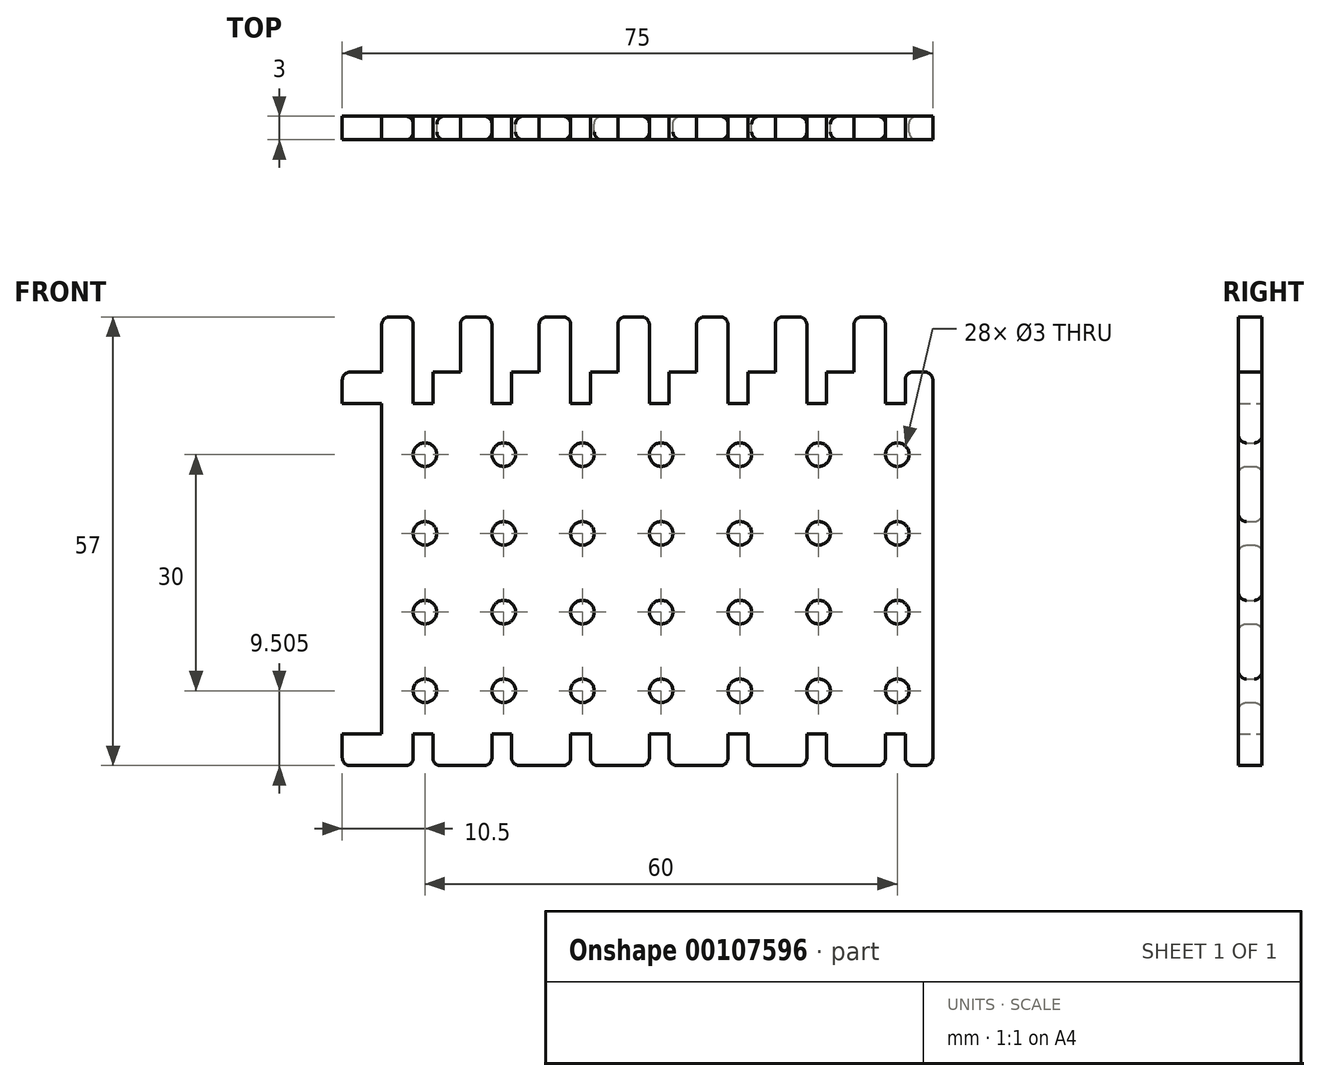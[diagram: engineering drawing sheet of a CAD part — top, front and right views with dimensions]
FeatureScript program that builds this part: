
annotation { "Feature Type Name" : "Feature", "Feature Type Description" : "" }
export const myFeature = defineFeature(function(context is Context, id is Id, definition is map)
    precondition{}
    {
        {
            var Q0;
            Q0=qCreatedBy(makeId("Front.planeOp"),FACE);
            var sketch = newSketch(context, id + "F0", { "sketchPlane" : qUnion([Q0])});
            skLineSegment(sketch, "E0.bottom", {"start": v(37.5, -25) * mm, "end": v(34, -25) * mm});
            skLineSegment(sketch, "E0.top", {"start": v(37.5, 25) * mm, "end": v(34, 25) * mm});
            skLineSegment(sketch, "E0.left", {"start": v(37.5, -25) * mm, "end": v(37.5, 25) * mm});
            skLineSegment(sketch, "E0.right", {"start": v(-37.5, -25) * mm, "end": v(-37.5, -21) * mm});
            skPoint(sketch, "E0.middle", {"position": v(0, 0) * mm});
            skLineSegment(sketch, "E1.top", {"start": v(-32.5, 32) * mm, "end": v(-28.5, 32) * mm});
            skLineSegment(sketch, "E1.left", {"start": v(-32.5, 25) * mm, "end": v(-32.5, 32) * mm});
            skLineSegment(sketch, "E1.right", {"start": v(-28.5, 25) * mm, "end": v(-28.5, 32) * mm});
            skLineSegment(sketch, "E2.top", {"start": v(-28.5, 21) * mm, "end": v(-26, 21) * mm});
            skLineSegment(sketch, "E2.left", {"start": v(-28.5, 25) * mm, "end": v(-28.5, 21) * mm});
            skLineSegment(sketch, "E2.right", {"start": v(-26, 25) * mm, "end": v(-26, 21) * mm});
            skLineSegment(sketch, "E3.top", {"start": v(-26, -21) * mm, "end": v(-28.5, -21) * mm});
            skLineSegment(sketch, "E3.left", {"start": v(-26, -25) * mm, "end": v(-26, -21) * mm});
            skLineSegment(sketch, "E3.right", {"start": v(-28.5, -25) * mm, "end": v(-28.5, -21) * mm});
            skLineSegment(sketch, "E4.bottom", {"start": v(-37.5, 21) * mm, "end": v(-32.5, 21) * mm});
            skLineSegment(sketch, "E4.top", {"start": v(-37.5, -21) * mm, "end": v(-32.5, -21) * mm});
            skLineSegment(sketch, "E4.right", {"start": v(-32.5, 21) * mm, "end": v(-32.5, -21) * mm});
            skLineSegment(sketch, "E5.trimOffspring", {"start": v(-37.5, 21) * mm, "end": v(-37.5, 25) * mm});
            skLineSegment(sketch, "E6.trimOffspring", {"start": v(-32.5, 25) * mm, "end": v(-37.5, 25) * mm});
            skLineSegment(sketch, "E7.trimOffspring", {"start": v(-28.5, -25) * mm, "end": v(-37.5, -25) * mm});
            skLineSegment(sketch, "E8.1.0.0", {"start": v(-22.5, 25) * mm, "end": v(-22.5, 32) * mm});
            skLineSegment(sketch, "E8.1.0.1", {"start": v(-22.5, 32) * mm, "end": v(-18.5, 32) * mm});
            skLineSegment(sketch, "E8.1.0.2", {"start": v(-18.5, 25) * mm, "end": v(-18.5, 32) * mm});
            skLineSegment(sketch, "E8.1.0.3", {"start": v(-18.5, 25) * mm, "end": v(-18.5, 21) * mm});
            skLineSegment(sketch, "E8.1.0.4", {"start": v(-16, 25) * mm, "end": v(-16, 21) * mm});
            skLineSegment(sketch, "E8.1.0.5", {"start": v(-18.5, -25) * mm, "end": v(-18.5, -21) * mm});
            skLineSegment(sketch, "E8.1.0.6", {"start": v(-16, -25) * mm, "end": v(-16, -21) * mm});
            skLineSegment(sketch, "E8.1.0.7", {"start": v(-16, -21) * mm, "end": v(-18.5, -21) * mm});
            skLineSegment(sketch, "E8.1.0.8", {"start": v(-18.5, 21) * mm, "end": v(-16, 21) * mm});
            skLineSegment(sketch, "E8.2.0.0", {"start": v(-12.5, 25) * mm, "end": v(-12.5, 32) * mm});
            skLineSegment(sketch, "E8.2.0.1", {"start": v(-12.5, 32) * mm, "end": v(-8.5, 32) * mm});
            skLineSegment(sketch, "E8.2.0.2", {"start": v(-8.5, 25) * mm, "end": v(-8.5, 32) * mm});
            skLineSegment(sketch, "E8.2.0.3", {"start": v(-8.5, 25) * mm, "end": v(-8.5, 21) * mm});
            skLineSegment(sketch, "E8.2.0.4", {"start": v(-6, 25) * mm, "end": v(-6, 21) * mm});
            skLineSegment(sketch, "E8.2.0.5", {"start": v(-8.5, -25) * mm, "end": v(-8.5, -21) * mm});
            skLineSegment(sketch, "E8.2.0.6", {"start": v(-6, -25) * mm, "end": v(-6, -21) * mm});
            skLineSegment(sketch, "E8.2.0.7", {"start": v(-6, -21) * mm, "end": v(-8.5, -21) * mm});
            skLineSegment(sketch, "E8.2.0.8", {"start": v(-8.5, 21) * mm, "end": v(-6, 21) * mm});
            skLineSegment(sketch, "E8.3.0.0", {"start": v(-2.5, 25) * mm, "end": v(-2.5, 32) * mm});
            skLineSegment(sketch, "E8.3.0.1", {"start": v(-2.5, 32) * mm, "end": v(1.5, 32) * mm});
            skLineSegment(sketch, "E8.3.0.2", {"start": v(1.5, 25) * mm, "end": v(1.5, 32) * mm});
            skLineSegment(sketch, "E8.3.0.3", {"start": v(1.5, 25) * mm, "end": v(1.5, 21) * mm});
            skLineSegment(sketch, "E8.3.0.4", {"start": v(4, 25) * mm, "end": v(4, 21) * mm});
            skLineSegment(sketch, "E8.3.0.5", {"start": v(1.5, -25) * mm, "end": v(1.5, -21) * mm});
            skLineSegment(sketch, "E8.3.0.6", {"start": v(4, -25) * mm, "end": v(4, -21) * mm});
            skLineSegment(sketch, "E8.3.0.7", {"start": v(4, -21) * mm, "end": v(1.5, -21) * mm});
            skLineSegment(sketch, "E8.3.0.8", {"start": v(1.5, 21) * mm, "end": v(4, 21) * mm});
            skLineSegment(sketch, "E8.4.0.0", {"start": v(7.5, 25) * mm, "end": v(7.5, 32) * mm});
            skLineSegment(sketch, "E8.4.0.1", {"start": v(7.5, 32) * mm, "end": v(11.5, 32) * mm});
            skLineSegment(sketch, "E8.4.0.2", {"start": v(11.5, 25) * mm, "end": v(11.5, 32) * mm});
            skLineSegment(sketch, "E8.4.0.3", {"start": v(11.5, 25) * mm, "end": v(11.5, 21) * mm});
            skLineSegment(sketch, "E8.4.0.4", {"start": v(14, 25) * mm, "end": v(14, 21) * mm});
            skLineSegment(sketch, "E8.4.0.5", {"start": v(11.5, -25) * mm, "end": v(11.5, -21) * mm});
            skLineSegment(sketch, "E8.4.0.6", {"start": v(14, -25) * mm, "end": v(14, -21) * mm});
            skLineSegment(sketch, "E8.4.0.7", {"start": v(14, -21) * mm, "end": v(11.5, -21) * mm});
            skLineSegment(sketch, "E8.4.0.8", {"start": v(11.5, 21) * mm, "end": v(14, 21) * mm});
            skLineSegment(sketch, "E8.5.0.0", {"start": v(17.5, 25) * mm, "end": v(17.5, 32) * mm});
            skLineSegment(sketch, "E8.5.0.1", {"start": v(17.5, 32) * mm, "end": v(21.5, 32) * mm});
            skLineSegment(sketch, "E8.5.0.2", {"start": v(21.5, 25) * mm, "end": v(21.5, 32) * mm});
            skLineSegment(sketch, "E8.5.0.3", {"start": v(21.5, 25) * mm, "end": v(21.5, 21) * mm});
            skLineSegment(sketch, "E8.5.0.4", {"start": v(24, 25) * mm, "end": v(24, 21) * mm});
            skLineSegment(sketch, "E8.5.0.5", {"start": v(21.5, -25) * mm, "end": v(21.5, -21) * mm});
            skLineSegment(sketch, "E8.5.0.6", {"start": v(24, -25) * mm, "end": v(24, -21) * mm});
            skLineSegment(sketch, "E8.5.0.7", {"start": v(24, -21) * mm, "end": v(21.5, -21) * mm});
            skLineSegment(sketch, "E8.5.0.8", {"start": v(21.5, 21) * mm, "end": v(24, 21) * mm});
            skLineSegment(sketch, "E8.6.0.0", {"start": v(27.5, 25) * mm, "end": v(27.5, 32) * mm});
            skLineSegment(sketch, "E8.6.0.1", {"start": v(27.5, 32) * mm, "end": v(31.5, 32) * mm});
            skLineSegment(sketch, "E8.6.0.2", {"start": v(31.5, 25) * mm, "end": v(31.5, 32) * mm});
            skLineSegment(sketch, "E8.6.0.3", {"start": v(31.5, 25) * mm, "end": v(31.5, 21) * mm});
            skLineSegment(sketch, "E8.6.0.4", {"start": v(34, 25) * mm, "end": v(34, 21) * mm});
            skLineSegment(sketch, "E8.6.0.5", {"start": v(31.5, -25) * mm, "end": v(31.5, -21) * mm});
            skLineSegment(sketch, "E8.6.0.6", {"start": v(34, -25) * mm, "end": v(34, -21) * mm});
            skLineSegment(sketch, "E8.6.0.7", {"start": v(34, -21) * mm, "end": v(31.5, -21) * mm});
            skLineSegment(sketch, "E8.6.0.8", {"start": v(31.5, 21) * mm, "end": v(34, 21) * mm});
            skLineSegment(sketch, "E8.direction1", {"start": v(-32.5, 25) * mm, "end": v(-22.5, 25) * mm, "construction": true});
            skLineSegment(sketch, "E9.trimOffspring", {"start": v(-22.5, 25) * mm, "end": v(-26, 25) * mm});
            skLineSegment(sketch, "E10.trimOffspring", {"start": v(-12.5, 25) * mm, "end": v(-16, 25) * mm});
            skLineSegment(sketch, "E11.trimOffspring", {"start": v(-2.5, 25) * mm, "end": v(-6, 25) * mm});
            skLineSegment(sketch, "E12.trimOffspring", {"start": v(7.5, 25) * mm, "end": v(4, 25) * mm});
            skLineSegment(sketch, "E13.trimOffspring", {"start": v(17.5, 25) * mm, "end": v(14, 25) * mm});
            skLineSegment(sketch, "E14.trimOffspring", {"start": v(27.5, 25) * mm, "end": v(24, 25) * mm});
            skLineSegment(sketch, "E15.trimOffspring", {"start": v(-18.5, -25) * mm, "end": v(-26, -25) * mm});
            skLineSegment(sketch, "E16.trimOffspring", {"start": v(-8.5, -25) * mm, "end": v(-16, -25) * mm});
            skLineSegment(sketch, "E17.trimOffspring", {"start": v(1.5, -25) * mm, "end": v(-6, -25) * mm});
            skLineSegment(sketch, "E18.trimOffspring", {"start": v(11.5, -25) * mm, "end": v(4, -25) * mm});
            skLineSegment(sketch, "E19.trimOffspring", {"start": v(21.5, -25) * mm, "end": v(14, -25) * mm});
            skLineSegment(sketch, "E20.trimOffspring", {"start": v(31.5, -25) * mm, "end": v(24, -25) * mm});
            skCircle(sketch, "E21", {"center": v(-27, 14.5) * mm, "radius": 1.5 * mm});
            skCircle(sketch, "E22.0.1.0", {"center": v(-27, 4.5) * mm, "radius": 1.5 * mm});
            skCircle(sketch, "E22.0.2.0", {"center": v(-27, -5.5) * mm, "radius": 1.5 * mm});
            skCircle(sketch, "E22.0.3.0", {"center": v(-27, -15.5) * mm, "radius": 1.5 * mm});
            skCircle(sketch, "E22.1.0.0", {"center": v(-17, 14.5) * mm, "radius": 1.5 * mm});
            skCircle(sketch, "E22.1.1.0", {"center": v(-17, 4.5) * mm, "radius": 1.5 * mm});
            skCircle(sketch, "E22.1.2.0", {"center": v(-17, -5.5) * mm, "radius": 1.5 * mm});
            skCircle(sketch, "E22.1.3.0", {"center": v(-17, -15.5) * mm, "radius": 1.5 * mm});
            skCircle(sketch, "E22.2.0.0", {"center": v(-7, 14.5) * mm, "radius": 1.5 * mm});
            skCircle(sketch, "E22.2.1.0", {"center": v(-7, 4.5) * mm, "radius": 1.5 * mm});
            skCircle(sketch, "E22.2.2.0", {"center": v(-7, -5.5) * mm, "radius": 1.5 * mm});
            skCircle(sketch, "E22.2.3.0", {"center": v(-7, -15.5) * mm, "radius": 1.5 * mm});
            skCircle(sketch, "E22.3.0.0", {"center": v(3, 14.5) * mm, "radius": 1.5 * mm});
            skCircle(sketch, "E22.3.1.0", {"center": v(3, 4.5) * mm, "radius": 1.5 * mm});
            skCircle(sketch, "E22.3.2.0", {"center": v(3, -5.5) * mm, "radius": 1.5 * mm});
            skCircle(sketch, "E22.3.3.0", {"center": v(3, -15.5) * mm, "radius": 1.5 * mm});
            skCircle(sketch, "E22.4.0.0", {"center": v(13, 14.5) * mm, "radius": 1.5 * mm});
            skCircle(sketch, "E22.4.1.0", {"center": v(13, 4.5) * mm, "radius": 1.5 * mm});
            skCircle(sketch, "E22.4.2.0", {"center": v(13, -5.5) * mm, "radius": 1.5 * mm});
            skCircle(sketch, "E22.4.3.0", {"center": v(13, -15.5) * mm, "radius": 1.5 * mm});
            skCircle(sketch, "E22.5.0.0", {"center": v(23, 14.5) * mm, "radius": 1.5 * mm});
            skCircle(sketch, "E22.5.1.0", {"center": v(23, 4.5) * mm, "radius": 1.5 * mm});
            skCircle(sketch, "E22.5.2.0", {"center": v(23, -5.5) * mm, "radius": 1.5 * mm});
            skCircle(sketch, "E22.5.3.0", {"center": v(23, -15.5) * mm, "radius": 1.5 * mm});
            skCircle(sketch, "E22.6.0.0", {"center": v(33, 14.5) * mm, "radius": 1.5 * mm});
            skCircle(sketch, "E22.6.1.0", {"center": v(33, 4.5) * mm, "radius": 1.5 * mm});
            skCircle(sketch, "E22.6.2.0", {"center": v(33, -5.5) * mm, "radius": 1.5 * mm});
            skCircle(sketch, "E22.6.3.0", {"center": v(33, -15.5) * mm, "radius": 1.5 * mm});
            skLineSegment(sketch, "E22.direction1", {"start": v(-27, 14.5) * mm, "end": v(-17, 14.5) * mm, "construction": true});
            skLineSegment(sketch, "E22.direction2", {"start": v(-27, 14.5) * mm, "end": v(-27, 4.5) * mm, "construction": true});
            skSolve(sketch);
        }
        {
            var Q0;
            Q0=makeQuery(id+"F0.imprint","IMPRINT",FACE,{"disambiguationData":[TD([[makeQuery(id+"F0.imprint","IMPRINT",EDGE,{"derivedFrom":sQuery(id+"F0.wireOp",EDGE,"E0.bottom")}),-1.0]])]});
            extrude(context, id + "F1", {"entities" : qUnion([Q0]), "depth" : 3 * mm});
        }
        {
            var Q0;
            Q0=makeQuery(id+"F1.opExtrude","SWEPT_EDGE",EDGE,{"disambiguationData":[OSD([sQuery(id+"F0.wireOp",EDGE,"E3.right"),sQuery(id+"F0.wireOp",EDGE,"E7.trimOffspring")])]});
            var Q1;
            Q1=makeQuery(id+"F1.opExtrude","SWEPT_EDGE",EDGE,{"disambiguationData":[OSD([sQuery(id+"F0.wireOp",EDGE,"E3.left"),sQuery(id+"F0.wireOp",EDGE,"E15.trimOffspring")])]});
            var Q2;
            Q2=makeQuery(id+"F1.opExtrude","SWEPT_EDGE",EDGE,{"disambiguationData":[OSD([sQuery(id+"F0.wireOp",EDGE,"E8.1.0.5"),sQuery(id+"F0.wireOp",EDGE,"E15.trimOffspring")])]});
            var Q3;
            Q3=makeQuery(id+"F1.opExtrude","SWEPT_EDGE",EDGE,{"disambiguationData":[OSD([sQuery(id+"F0.wireOp",EDGE,"E8.1.0.6"),sQuery(id+"F0.wireOp",EDGE,"E16.trimOffspring")])]});
            var Q4;
            Q4=makeQuery(id+"F1.opExtrude","SWEPT_EDGE",EDGE,{"disambiguationData":[OSD([sQuery(id+"F0.wireOp",EDGE,"E8.2.0.5"),sQuery(id+"F0.wireOp",EDGE,"E16.trimOffspring")])]});
            var Q5;
            Q5=makeQuery(id+"F1.opExtrude","SWEPT_EDGE",EDGE,{"disambiguationData":[OSD([sQuery(id+"F0.wireOp",EDGE,"E8.2.0.6"),sQuery(id+"F0.wireOp",EDGE,"E17.trimOffspring")])]});
            var Q6;
            Q6=makeQuery(id+"F1.opExtrude","SWEPT_EDGE",EDGE,{"disambiguationData":[OSD([sQuery(id+"F0.wireOp",EDGE,"E8.3.0.5"),sQuery(id+"F0.wireOp",EDGE,"E17.trimOffspring")])]});
            var Q7;
            Q7=makeQuery(id+"F1.opExtrude","SWEPT_EDGE",EDGE,{"disambiguationData":[OSD([sQuery(id+"F0.wireOp",EDGE,"E8.3.0.6"),sQuery(id+"F0.wireOp",EDGE,"E18.trimOffspring")])]});
            var Q8;
            Q8=makeQuery(id+"F1.opExtrude","SWEPT_EDGE",EDGE,{"disambiguationData":[OSD([sQuery(id+"F0.wireOp",EDGE,"E8.4.0.5"),sQuery(id+"F0.wireOp",EDGE,"E18.trimOffspring")])]});
            var Q9;
            Q9=makeQuery(id+"F1.opExtrude","SWEPT_EDGE",EDGE,{"disambiguationData":[OSD([sQuery(id+"F0.wireOp",EDGE,"E8.4.0.6"),sQuery(id+"F0.wireOp",EDGE,"E19.trimOffspring")])]});
            var Q10;
            Q10=makeQuery(id+"F1.opExtrude","SWEPT_EDGE",EDGE,{"disambiguationData":[OSD([sQuery(id+"F0.wireOp",EDGE,"E8.5.0.5"),sQuery(id+"F0.wireOp",EDGE,"E19.trimOffspring")])]});
            var Q11;
            Q11=makeQuery(id+"F1.opExtrude","SWEPT_EDGE",EDGE,{"disambiguationData":[OSD([sQuery(id+"F0.wireOp",EDGE,"E8.5.0.6"),sQuery(id+"F0.wireOp",EDGE,"E20.trimOffspring")])]});
            var Q12;
            Q12=makeQuery(id+"F1.opExtrude","SWEPT_EDGE",EDGE,{"disambiguationData":[OSD([sQuery(id+"F0.wireOp",EDGE,"E8.6.0.5"),sQuery(id+"F0.wireOp",EDGE,"E20.trimOffspring")])]});
            var Q13;
            Q13=makeQuery(id+"F1.opExtrude","SWEPT_EDGE",EDGE,{"disambiguationData":[OSD([sQuery(id+"F0.wireOp",EDGE,"E0.bottom"),sQuery(id+"F0.wireOp",EDGE,"E8.6.0.6")])]});
            var Q14;
            Q14=makeQuery(id+"F1.opExtrude","SWEPT_EDGE",EDGE,{"disambiguationData":[OSD([sQuery(id+"F0.wireOp",EDGE,"E0.bottom"),sQuery(id+"F0.wireOp",EDGE,"E0.left")])]});
            var Q15;
            Q15=makeQuery(id+"F1.opExtrude","SWEPT_EDGE",EDGE,{"disambiguationData":[OSD([sQuery(id+"F0.wireOp",EDGE,"E0.right"),sQuery(id+"F0.wireOp",EDGE,"E7.trimOffspring")])]});
            var Q16;
            Q16=makeQuery(id+"F1.opExtrude","SWEPT_EDGE",EDGE,{"disambiguationData":[OSD([sQuery(id+"F0.wireOp",EDGE,"E8.6.0.1"),sQuery(id+"F0.wireOp",EDGE,"E8.6.0.2")])]});
            var Q17;
            Q17=makeQuery(id+"F1.opExtrude","SWEPT_EDGE",EDGE,{"disambiguationData":[OSD([sQuery(id+"F0.wireOp",EDGE,"E8.6.0.0"),sQuery(id+"F0.wireOp",EDGE,"E8.6.0.1")])]});
            var Q18;
            Q18=makeQuery(id+"F1.opExtrude","SWEPT_EDGE",EDGE,{"disambiguationData":[OSD([sQuery(id+"F0.wireOp",EDGE,"E0.top"),sQuery(id+"F0.wireOp",EDGE,"E0.left")])]});
            var Q19;
            Q19=makeQuery(id+"F1.opExtrude","SWEPT_EDGE",EDGE,{"disambiguationData":[OSD([sQuery(id+"F0.wireOp",EDGE,"E0.top"),sQuery(id+"F0.wireOp",EDGE,"E8.6.0.4")])]});
            var Q20;
            Q20=makeQuery(id+"F1.opExtrude","SWEPT_EDGE",EDGE,{"disambiguationData":[OSD([sQuery(id+"F0.wireOp",EDGE,"E8.5.0.1"),sQuery(id+"F0.wireOp",EDGE,"E8.5.0.2")])]});
            var Q21;
            Q21=makeQuery(id+"F1.opExtrude","SWEPT_EDGE",EDGE,{"disambiguationData":[OSD([sQuery(id+"F0.wireOp",EDGE,"E8.5.0.0"),sQuery(id+"F0.wireOp",EDGE,"E8.5.0.1")])]});
            var Q22;
            Q22=makeQuery(id+"F1.opExtrude","SWEPT_EDGE",EDGE,{"disambiguationData":[OSD([sQuery(id+"F0.wireOp",EDGE,"E8.4.0.1"),sQuery(id+"F0.wireOp",EDGE,"E8.4.0.2")])]});
            var Q23;
            Q23=makeQuery(id+"F1.opExtrude","SWEPT_EDGE",EDGE,{"disambiguationData":[OSD([sQuery(id+"F0.wireOp",EDGE,"E8.4.0.0"),sQuery(id+"F0.wireOp",EDGE,"E8.4.0.1")])]});
            var Q24;
            Q24=makeQuery(id+"F1.opExtrude","SWEPT_EDGE",EDGE,{"disambiguationData":[OSD([sQuery(id+"F0.wireOp",EDGE,"E8.3.0.1"),sQuery(id+"F0.wireOp",EDGE,"E8.3.0.2")])]});
            var Q25;
            Q25=makeQuery(id+"F1.opExtrude","SWEPT_EDGE",EDGE,{"disambiguationData":[OSD([sQuery(id+"F0.wireOp",EDGE,"E8.3.0.0"),sQuery(id+"F0.wireOp",EDGE,"E8.3.0.1")])]});
            var Q26;
            Q26=makeQuery(id+"F1.opExtrude","SWEPT_EDGE",EDGE,{"disambiguationData":[OSD([sQuery(id+"F0.wireOp",EDGE,"E8.2.0.1"),sQuery(id+"F0.wireOp",EDGE,"E8.2.0.2")])]});
            var Q27;
            Q27=makeQuery(id+"F1.opExtrude","SWEPT_EDGE",EDGE,{"disambiguationData":[OSD([sQuery(id+"F0.wireOp",EDGE,"E8.2.0.0"),sQuery(id+"F0.wireOp",EDGE,"E8.2.0.1")])]});
            var Q28;
            Q28=makeQuery(id+"F1.opExtrude","SWEPT_EDGE",EDGE,{"disambiguationData":[OSD([sQuery(id+"F0.wireOp",EDGE,"E8.1.0.1"),sQuery(id+"F0.wireOp",EDGE,"E8.1.0.2")])]});
            var Q29;
            Q29=makeQuery(id+"F1.opExtrude","SWEPT_EDGE",EDGE,{"disambiguationData":[OSD([sQuery(id+"F0.wireOp",EDGE,"E8.1.0.0"),sQuery(id+"F0.wireOp",EDGE,"E8.1.0.1")])]});
            var Q30;
            Q30=makeQuery(id+"F1.opExtrude","SWEPT_EDGE",EDGE,{"disambiguationData":[OSD([sQuery(id+"F0.wireOp",EDGE,"E1.top"),sQuery(id+"F0.wireOp",EDGE,"E1.right")])]});
            var Q31;
            Q31=makeQuery(id+"F1.opExtrude","SWEPT_EDGE",EDGE,{"disambiguationData":[OSD([sQuery(id+"F0.wireOp",EDGE,"E1.top"),sQuery(id+"F0.wireOp",EDGE,"E1.left")])]});
            var Q32;
            Q32=makeQuery(id+"F1.opExtrude","SWEPT_EDGE",EDGE,{"disambiguationData":[OSD([sQuery(id+"F0.wireOp",EDGE,"E5.trimOffspring"),sQuery(id+"F0.wireOp",EDGE,"E6.trimOffspring")])]});
            var Q33;
            Q33=makeQuery(id+"F1.opExtrude","CAP_EDGE",EDGE,{"disambiguationData":[OSD([sQuery(id+"F0.wireOp",EDGE,"E22.6.0.0")])],"isStart":true});
            var Q34;
            Q34=makeQuery(id+"F1.opExtrude","CAP_EDGE",EDGE,{"disambiguationData":[OSD([sQuery(id+"F0.wireOp",EDGE,"E22.6.0.0")])],"isStart":false});
            var Q35;
            Q35=makeQuery(id+"F1.opExtrude","CAP_EDGE",EDGE,{"disambiguationData":[OSD([sQuery(id+"F0.wireOp",EDGE,"E22.6.1.0")])],"isStart":false});
            var Q36;
            Q36=makeQuery(id+"F1.opExtrude","CAP_EDGE",EDGE,{"disambiguationData":[OSD([sQuery(id+"F0.wireOp",EDGE,"E22.6.2.0")])],"isStart":false});
            var Q37;
            Q37=makeQuery(id+"F1.opExtrude","CAP_EDGE",EDGE,{"disambiguationData":[OSD([sQuery(id+"F0.wireOp",EDGE,"E22.6.3.0")])],"isStart":false});
            var Q38;
            Q38=makeQuery(id+"F1.opExtrude","CAP_EDGE",EDGE,{"disambiguationData":[OSD([sQuery(id+"F0.wireOp",EDGE,"E22.5.2.0")])],"isStart":false});
            var Q39;
            Q39=makeQuery(id+"F1.opExtrude","CAP_EDGE",EDGE,{"disambiguationData":[OSD([sQuery(id+"F0.wireOp",EDGE,"E22.5.3.0")])],"isStart":false});
            var Q40;
            Q40=makeQuery(id+"F1.opExtrude","CAP_EDGE",EDGE,{"disambiguationData":[OSD([sQuery(id+"F0.wireOp",EDGE,"E22.5.1.0")])],"isStart":false});
            var Q41;
            Q41=makeQuery(id+"F1.opExtrude","CAP_EDGE",EDGE,{"disambiguationData":[OSD([sQuery(id+"F0.wireOp",EDGE,"E22.5.0.0")])],"isStart":false});
            var Q42;
            Q42=makeQuery(id+"F1.opExtrude","CAP_EDGE",EDGE,{"disambiguationData":[OSD([sQuery(id+"F0.wireOp",EDGE,"E22.4.0.0")])],"isStart":false});
            var Q43;
            Q43=makeQuery(id+"F1.opExtrude","CAP_EDGE",EDGE,{"disambiguationData":[OSD([sQuery(id+"F0.wireOp",EDGE,"E22.4.1.0")])],"isStart":false});
            var Q44;
            Q44=makeQuery(id+"F1.opExtrude","CAP_EDGE",EDGE,{"disambiguationData":[OSD([sQuery(id+"F0.wireOp",EDGE,"E22.4.2.0")])],"isStart":false});
            var Q45;
            Q45=makeQuery(id+"F1.opExtrude","CAP_EDGE",EDGE,{"disambiguationData":[OSD([sQuery(id+"F0.wireOp",EDGE,"E22.4.3.0")])],"isStart":false});
            var Q46;
            Q46=makeQuery(id+"F1.opExtrude","CAP_EDGE",EDGE,{"disambiguationData":[OSD([sQuery(id+"F0.wireOp",EDGE,"E22.3.0.0")])],"isStart":false});
            var Q47;
            Q47=makeQuery(id+"F1.opExtrude","CAP_EDGE",EDGE,{"disambiguationData":[OSD([sQuery(id+"F0.wireOp",EDGE,"E22.3.1.0")])],"isStart":false});
            var Q48;
            Q48=makeQuery(id+"F1.opExtrude","CAP_EDGE",EDGE,{"disambiguationData":[OSD([sQuery(id+"F0.wireOp",EDGE,"E22.3.2.0")])],"isStart":false});
            var Q49;
            Q49=makeQuery(id+"F1.opExtrude","CAP_EDGE",EDGE,{"disambiguationData":[OSD([sQuery(id+"F0.wireOp",EDGE,"E22.3.3.0")])],"isStart":false});
            var Q50;
            Q50=makeQuery(id+"F1.opExtrude","CAP_EDGE",EDGE,{"disambiguationData":[OSD([sQuery(id+"F0.wireOp",EDGE,"E22.2.0.0")])],"isStart":false});
            var Q51;
            Q51=makeQuery(id+"F1.opExtrude","CAP_EDGE",EDGE,{"disambiguationData":[OSD([sQuery(id+"F0.wireOp",EDGE,"E22.2.1.0")])],"isStart":false});
            var Q52;
            Q52=makeQuery(id+"F1.opExtrude","CAP_EDGE",EDGE,{"disambiguationData":[OSD([sQuery(id+"F0.wireOp",EDGE,"E22.2.2.0")])],"isStart":false});
            var Q53;
            Q53=makeQuery(id+"F1.opExtrude","CAP_EDGE",EDGE,{"disambiguationData":[OSD([sQuery(id+"F0.wireOp",EDGE,"E22.2.3.0")])],"isStart":false});
            var Q54;
            Q54=makeQuery(id+"F1.opExtrude","CAP_EDGE",EDGE,{"disambiguationData":[OSD([sQuery(id+"F0.wireOp",EDGE,"E22.1.0.0")])],"isStart":false});
            var Q55;
            Q55=makeQuery(id+"F1.opExtrude","CAP_EDGE",EDGE,{"disambiguationData":[OSD([sQuery(id+"F0.wireOp",EDGE,"E22.1.1.0")])],"isStart":false});
            var Q56;
            Q56=makeQuery(id+"F1.opExtrude","CAP_EDGE",EDGE,{"disambiguationData":[OSD([sQuery(id+"F0.wireOp",EDGE,"E22.1.2.0")])],"isStart":false});
            var Q57;
            Q57=makeQuery(id+"F1.opExtrude","CAP_EDGE",EDGE,{"disambiguationData":[OSD([sQuery(id+"F0.wireOp",EDGE,"E22.1.3.0")])],"isStart":false});
            var Q58;
            Q58=makeQuery(id+"F1.opExtrude","CAP_EDGE",EDGE,{"disambiguationData":[OSD([sQuery(id+"F0.wireOp",EDGE,"E21")])],"isStart":false});
            var Q59;
            Q59=makeQuery(id+"F1.opExtrude","CAP_EDGE",EDGE,{"disambiguationData":[OSD([sQuery(id+"F0.wireOp",EDGE,"E22.0.1.0")])],"isStart":false});
            var Q60;
            Q60=makeQuery(id+"F1.opExtrude","CAP_EDGE",EDGE,{"disambiguationData":[OSD([sQuery(id+"F0.wireOp",EDGE,"E22.0.2.0")])],"isStart":false});
            var Q61;
            Q61=makeQuery(id+"F1.opExtrude","CAP_EDGE",EDGE,{"disambiguationData":[OSD([sQuery(id+"F0.wireOp",EDGE,"E22.0.3.0")])],"isStart":false});
            var Q62;
            Q62=makeQuery(id+"F1.opExtrude","CAP_EDGE",EDGE,{"disambiguationData":[OSD([sQuery(id+"F0.wireOp",EDGE,"E22.6.3.0")])],"isStart":true});
            var Q63;
            Q63=makeQuery(id+"F1.opExtrude","CAP_EDGE",EDGE,{"disambiguationData":[OSD([sQuery(id+"F0.wireOp",EDGE,"E22.6.2.0")])],"isStart":true});
            var Q64;
            Q64=makeQuery(id+"F1.opExtrude","CAP_EDGE",EDGE,{"disambiguationData":[OSD([sQuery(id+"F0.wireOp",EDGE,"E22.6.1.0")])],"isStart":true});
            var Q65;
            Q65=makeQuery(id+"F1.opExtrude","CAP_EDGE",EDGE,{"disambiguationData":[OSD([sQuery(id+"F0.wireOp",EDGE,"E22.5.3.0")])],"isStart":true});
            var Q66;
            Q66=makeQuery(id+"F1.opExtrude","CAP_EDGE",EDGE,{"disambiguationData":[OSD([sQuery(id+"F0.wireOp",EDGE,"E22.5.2.0")])],"isStart":true});
            var Q67;
            Q67=makeQuery(id+"F1.opExtrude","CAP_EDGE",EDGE,{"disambiguationData":[OSD([sQuery(id+"F0.wireOp",EDGE,"E22.5.1.0")])],"isStart":true});
            var Q68;
            Q68=makeQuery(id+"F1.opExtrude","CAP_EDGE",EDGE,{"disambiguationData":[OSD([sQuery(id+"F0.wireOp",EDGE,"E22.5.0.0")])],"isStart":true});
            var Q69;
            Q69=makeQuery(id+"F1.opExtrude","CAP_EDGE",EDGE,{"disambiguationData":[OSD([sQuery(id+"F0.wireOp",EDGE,"E22.4.0.0")])],"isStart":true});
            var Q70;
            Q70=makeQuery(id+"F1.opExtrude","CAP_EDGE",EDGE,{"disambiguationData":[OSD([sQuery(id+"F0.wireOp",EDGE,"E22.4.1.0")])],"isStart":true});
            var Q71;
            Q71=makeQuery(id+"F1.opExtrude","CAP_EDGE",EDGE,{"disambiguationData":[OSD([sQuery(id+"F0.wireOp",EDGE,"E22.4.2.0")])],"isStart":true});
            var Q72;
            Q72=makeQuery(id+"F1.opExtrude","CAP_EDGE",EDGE,{"disambiguationData":[OSD([sQuery(id+"F0.wireOp",EDGE,"E22.4.3.0")])],"isStart":true});
            var Q73;
            Q73=makeQuery(id+"F1.opExtrude","CAP_EDGE",EDGE,{"disambiguationData":[OSD([sQuery(id+"F0.wireOp",EDGE,"E22.3.3.0")])],"isStart":true});
            var Q74;
            Q74=makeQuery(id+"F1.opExtrude","CAP_EDGE",EDGE,{"disambiguationData":[OSD([sQuery(id+"F0.wireOp",EDGE,"E22.3.2.0")])],"isStart":true});
            var Q75;
            Q75=makeQuery(id+"F1.opExtrude","CAP_EDGE",EDGE,{"disambiguationData":[OSD([sQuery(id+"F0.wireOp",EDGE,"E22.3.1.0")])],"isStart":true});
            var Q76;
            Q76=makeQuery(id+"F1.opExtrude","CAP_EDGE",EDGE,{"disambiguationData":[OSD([sQuery(id+"F0.wireOp",EDGE,"E22.3.0.0")])],"isStart":true});
            var Q77;
            Q77=makeQuery(id+"F1.opExtrude","CAP_EDGE",EDGE,{"disambiguationData":[OSD([sQuery(id+"F0.wireOp",EDGE,"E22.2.3.0")])],"isStart":true});
            var Q78;
            Q78=makeQuery(id+"F1.opExtrude","CAP_EDGE",EDGE,{"disambiguationData":[OSD([sQuery(id+"F0.wireOp",EDGE,"E22.2.2.0")])],"isStart":true});
            var Q79;
            Q79=makeQuery(id+"F1.opExtrude","CAP_EDGE",EDGE,{"disambiguationData":[OSD([sQuery(id+"F0.wireOp",EDGE,"E22.2.1.0")])],"isStart":true});
            var Q80;
            Q80=makeQuery(id+"F1.opExtrude","CAP_EDGE",EDGE,{"disambiguationData":[OSD([sQuery(id+"F0.wireOp",EDGE,"E22.2.0.0")])],"isStart":true});
            var Q81;
            Q81=makeQuery(id+"F1.opExtrude","CAP_EDGE",EDGE,{"disambiguationData":[OSD([sQuery(id+"F0.wireOp",EDGE,"E22.1.0.0")])],"isStart":true});
            var Q82;
            Q82=makeQuery(id+"F1.opExtrude","CAP_EDGE",EDGE,{"disambiguationData":[OSD([sQuery(id+"F0.wireOp",EDGE,"E22.1.1.0")])],"isStart":true});
            var Q83;
            Q83=makeQuery(id+"F1.opExtrude","CAP_EDGE",EDGE,{"disambiguationData":[OSD([sQuery(id+"F0.wireOp",EDGE,"E22.1.2.0")])],"isStart":true});
            var Q84;
            Q84=makeQuery(id+"F1.opExtrude","CAP_EDGE",EDGE,{"disambiguationData":[OSD([sQuery(id+"F0.wireOp",EDGE,"E22.1.3.0")])],"isStart":true});
            var Q85;
            Q85=makeQuery(id+"F1.opExtrude","CAP_EDGE",EDGE,{"disambiguationData":[OSD([sQuery(id+"F0.wireOp",EDGE,"E22.0.3.0")])],"isStart":true});
            var Q86;
            Q86=makeQuery(id+"F1.opExtrude","CAP_EDGE",EDGE,{"disambiguationData":[OSD([sQuery(id+"F0.wireOp",EDGE,"E22.0.2.0")])],"isStart":true});
            var Q87;
            Q87=makeQuery(id+"F1.opExtrude","CAP_EDGE",EDGE,{"disambiguationData":[OSD([sQuery(id+"F0.wireOp",EDGE,"E22.0.1.0")])],"isStart":true});
            var Q88;
            Q88=makeQuery(id+"F1.opExtrude","CAP_EDGE",EDGE,{"disambiguationData":[OSD([sQuery(id+"F0.wireOp",EDGE,"E21")])],"isStart":true});
            fillet(context, id + "F2", {"entities" : qUnion([Q0, Q1, Q2, Q3, Q4, Q5, Q6, Q7, Q8, Q9, Q10, Q11, Q12, Q13, Q14, Q15, Q16, Q17, Q18, Q19, Q20, Q21, Q22, Q23, Q24, Q25, Q26, Q27, Q28, Q29, Q30, Q31, Q32, Q33, Q34, Q35, Q36, Q37, Q38, Q39, Q40, Q41, Q42, Q43, Q44, Q45, Q46, Q47, Q48, Q49, Q50, Q51, Q52, Q53, Q54, Q55, Q56, Q57, Q58, Q59, Q60, Q61, Q62, Q63, Q64, Q65, Q66, Q67, Q68, Q69, Q70, Q71, Q72, Q73, Q74, Q75, Q76, Q77, Q78, Q79, Q80, Q81, Q82, Q83, Q84, Q85, Q86, Q87, Q88]), "radius" : 1 * mm, "allowEdgeOverflow" : false});
        }
    });
